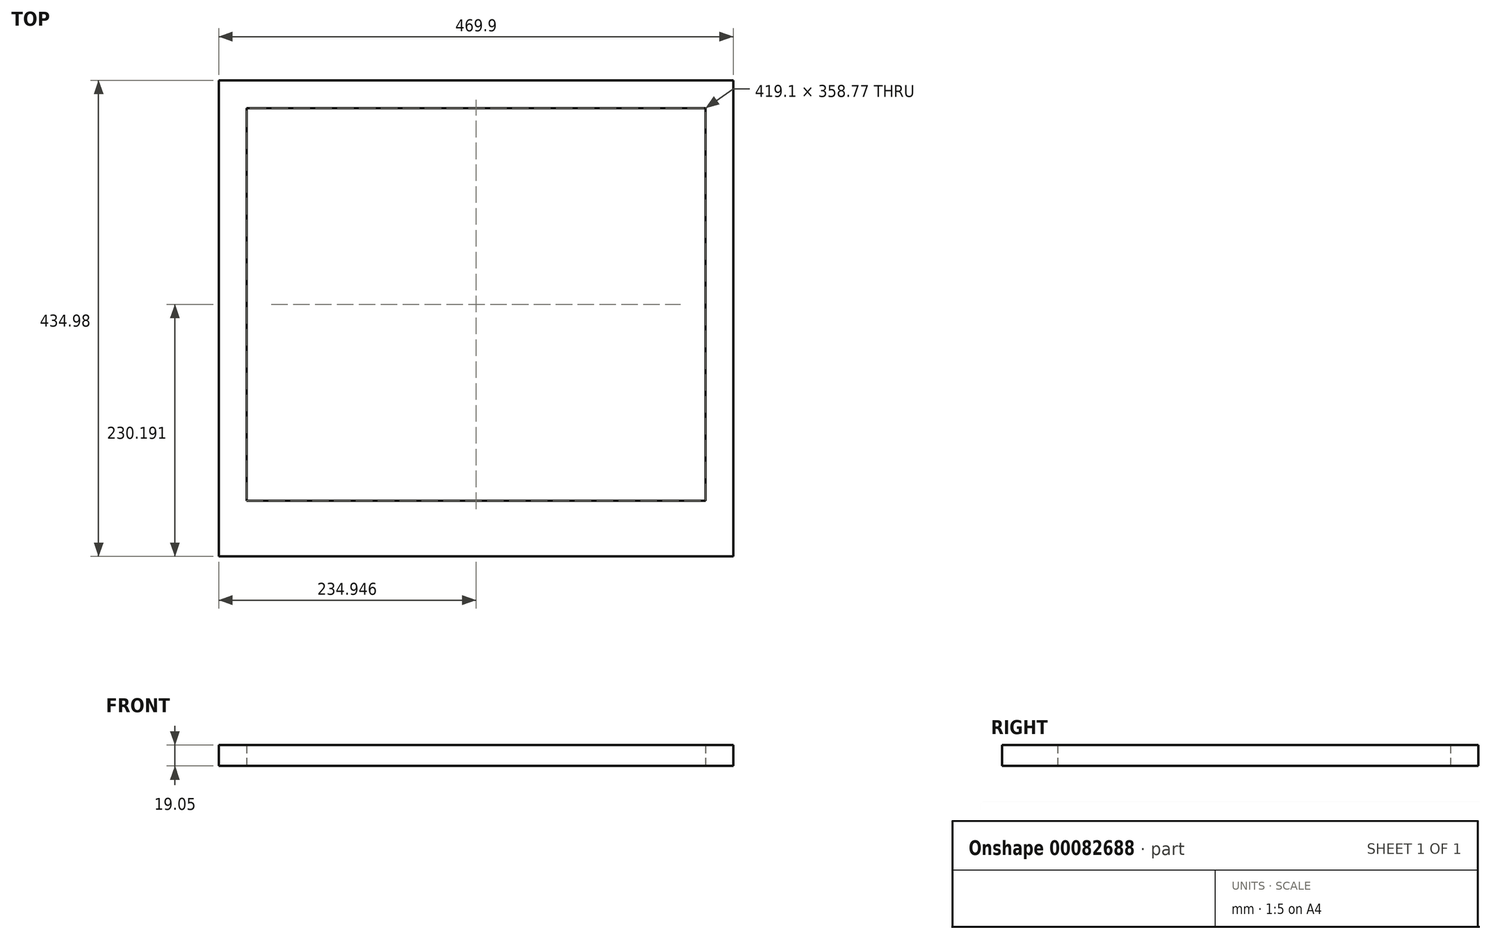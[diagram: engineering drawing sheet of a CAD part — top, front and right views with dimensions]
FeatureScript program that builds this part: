
annotation { "Feature Type Name" : "Feature", "Feature Type Description" : "" }
export const myFeature = defineFeature(function(context is Context, id is Id, definition is map)
    precondition{}
    {
        {
            var Q0;
            Q0=qCreatedBy(makeId("Top.planeOp"),FACE);
            var sketch = newSketch(context, id + "F0", { "sketchPlane" : qUnion([Q0])});
            skLineSegment(sketch, "E0.bottom", {"start": v(-219.22, 266.89) * mm, "end": v(250.68, 266.89) * mm});
            skLineSegment(sketch, "E0.top", {"start": v(-219.22, -168.09) * mm, "end": v(250.68, -168.09) * mm});
            skLineSegment(sketch, "E0.left", {"start": v(-219.22, 266.89) * mm, "end": v(-219.22, -168.09) * mm});
            skLineSegment(sketch, "E0.right", {"start": v(250.68, 266.89) * mm, "end": v(250.68, -168.09) * mm});
            skLineSegment(sketch, "E1.0", {"start": v(225.28, 241.49) * mm, "end": v(225.28, -117.29) * mm});
            skLineSegment(sketch, "E1.1", {"start": v(-193.82, 241.49) * mm, "end": v(225.28, 241.49) * mm});
            skLineSegment(sketch, "E1.2", {"start": v(-193.82, 241.49) * mm, "end": v(-193.82, -117.29) * mm});
            skLineSegment(sketch, "E2.0", {"start": v(-193.82, -117.29) * mm, "end": v(225.28, -117.29) * mm});
            skSolve(sketch);
        }
        {
            var Q0;
            Q0=qSketchRegion(id+"F0",true);
            extrude(context, id + "F1", {"entities" : qUnion([Q0]), "depth" : 19.05 * mm});
        }
    });
